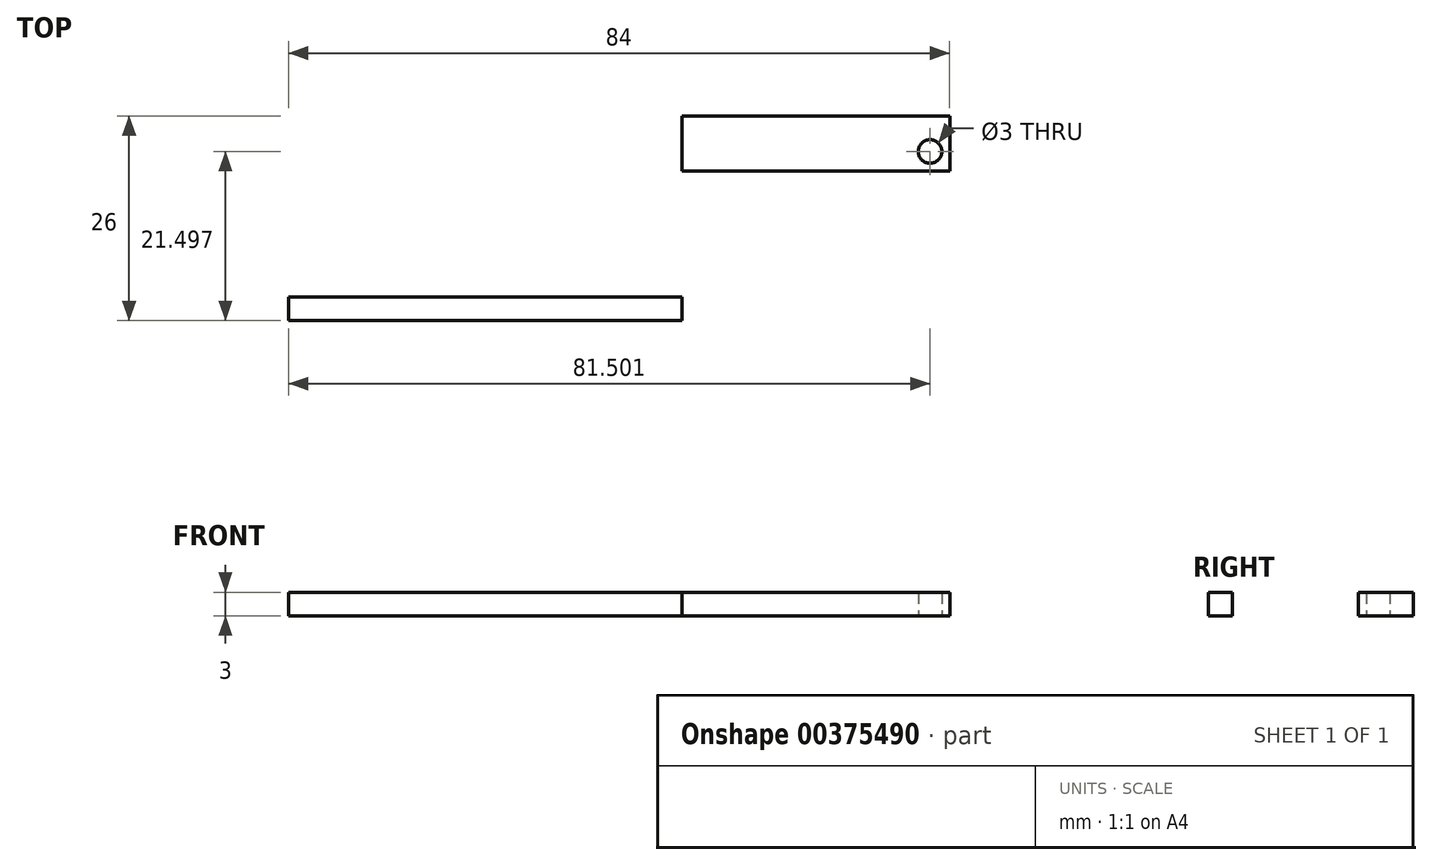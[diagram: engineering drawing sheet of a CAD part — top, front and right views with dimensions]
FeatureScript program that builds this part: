
annotation { "Feature Type Name" : "Feature", "Feature Type Description" : "" }
export const myFeature = defineFeature(function(context is Context, id is Id, definition is map)
    precondition{}
    {
        {
            var Q0;
            Q0=qCreatedBy(makeId("Top.planeOp"),FACE);
            var sketch = newSketch(context, id + "F0", { "sketchPlane" : qUnion([Q0])});
            skLineSegment(sketch, "E0.bottom", {"start": v(-37.1, -15.01) * mm, "end": v(15.9, -15.01) * mm});
            skLineSegment(sketch, "E0.top", {"start": v(-37.1, 10.99) * mm, "end": v(15.9, 10.99) * mm});
            skLineSegment(sketch, "E0.left", {"start": v(-37.1, -15.01) * mm, "end": v(-37.1, 10.99) * mm});
            skLineSegment(sketch, "E0.right", {"start": v(15.9, -15.01) * mm, "end": v(15.9, 10.99) * mm});
            skLineSegment(sketch, "E1.bottom", {"start": v(-34.1, -15.01) * mm, "end": v(15.9, -15.01) * mm});
            skLineSegment(sketch, "E1.top", {"start": v(-34.1, -12.01) * mm, "end": v(15.9, -12.01) * mm});
            skLineSegment(sketch, "E1.left", {"start": v(-34.1, -15.01) * mm, "end": v(-34.1, -12.01) * mm});
            skLineSegment(sketch, "E1.right", {"start": v(15.9, -15.01) * mm, "end": v(15.9, -12.01) * mm});
            skLineSegment(sketch, "E2.bottom", {"start": v(10.9, 10.99) * mm, "end": v(-12.1, 10.99) * mm});
            skLineSegment(sketch, "E2.top", {"start": v(10.9, -2.01) * mm, "end": v(-12.1, -2.01) * mm});
            skLineSegment(sketch, "E2.left", {"start": v(10.9, 10.99) * mm, "end": v(10.9, -2.01) * mm});
            skLineSegment(sketch, "E2.right", {"start": v(-12.1, 10.99) * mm, "end": v(-12.1, -2.01) * mm});
            skLineSegment(sketch, "E3.bottom", {"start": v(-37.1, 1.99) * mm, "end": v(-22.1, 1.99) * mm});
            skLineSegment(sketch, "E3.top", {"start": v(-37.1, -0.01) * mm, "end": v(-22.1, -0.01) * mm});
            skLineSegment(sketch, "E3.left", {"start": v(-37.1, 1.99) * mm, "end": v(-37.1, -0.01) * mm});
            skLineSegment(sketch, "E3.right", {"start": v(-22.1, 1.99) * mm, "end": v(-22.1, -0.01) * mm});
            skLineSegment(sketch, "E4.bottom", {"start": v(-22, -2.01) * mm, "end": v(-28, -2.01) * mm});
            skLineSegment(sketch, "E4.top", {"start": v(-22, 2.99) * mm, "end": v(-28, 2.99) * mm});
            skLineSegment(sketch, "E4.left", {"start": v(-22, -2.01) * mm, "end": v(-22, 2.99) * mm});
            skLineSegment(sketch, "E4.right", {"start": v(-28, -2.01) * mm, "end": v(-28, 2.99) * mm});
            skLineSegment(sketch, "E5.bottom", {"start": v(-37.1, 6.99) * mm, "end": v(-33.1, 6.99) * mm});
            skLineSegment(sketch, "E5.top", {"start": v(-37.1, -3.01) * mm, "end": v(-33.1, -3.01) * mm});
            skLineSegment(sketch, "E5.left", {"start": v(-37.1, 6.99) * mm, "end": v(-37.1, -3.01) * mm});
            skLineSegment(sketch, "E5.right", {"start": v(-33.1, 6.99) * mm, "end": v(-33.1, -3.01) * mm});
            skLineSegment(sketch, "E6.bottom", {"start": v(15.9, 3.99) * mm, "end": v(49.9, 3.99) * mm});
            skLineSegment(sketch, "E6.top", {"start": v(15.9, 10.99) * mm, "end": v(49.9, 10.99) * mm});
            skLineSegment(sketch, "E6.left", {"start": v(15.9, 3.99) * mm, "end": v(15.9, 10.99) * mm});
            skLineSegment(sketch, "E6.right", {"start": v(49.9, 3.99) * mm, "end": v(49.9, 10.99) * mm});
            skCircle(sketch, "E7", {"center": v(47.4, 6.49) * mm, "radius": 1.5 * mm});
            skCircle(sketch, "E8", {"center": v(13.4, 4.49) * mm, "radius": 1.5 * mm});
            skCircle(sketch, "E9", {"center": v(-14.6, 3.49) * mm, "radius": 1.5 * mm});
            skSolve(sketch);
        }
        {
            var Q0;
            Q0=makeQuery(id+"F0.imprint","IMPRINT",FACE,{"disambiguationData":[TD([[makeQuery(id+"F0.imprint","IMPRINT",EDGE,{"derivedFrom":sQuery(id+"F0.wireOp",EDGE,"E0.bottom")}),1.0]])]});
            var Q1;
            Q1=makeQuery(id+"F0.imprint","IMPRINT",FACE,{"disambiguationData":[TD([[makeQuery(id+"F0.imprint","IMPRINT",EDGE,{"derivedFrom":sQuery(id+"F0.wireOp",EDGE,"E6.bottom")}),1.0]])]});
            extrude(context, id + "F1", {"entities" : qUnion([Q0, Q1]), "depth" : 3 * mm});
        }
    });
